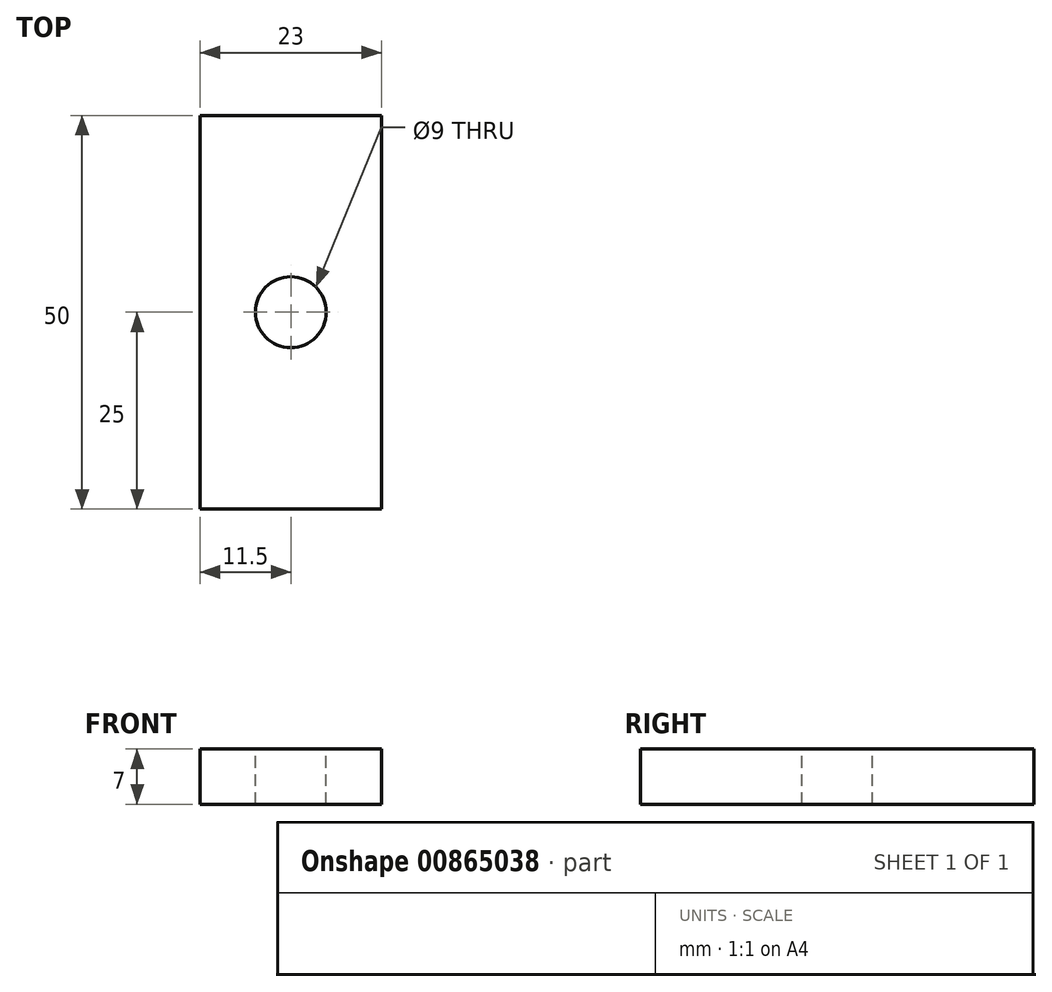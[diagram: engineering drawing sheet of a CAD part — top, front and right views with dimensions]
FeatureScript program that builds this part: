
annotation { "Feature Type Name" : "Feature", "Feature Type Description" : "" }
export const myFeature = defineFeature(function(context is Context, id is Id, definition is map)
    precondition{}
    {
        {
            var Q0;
            Q0=qCreatedBy(makeId("Top.planeOp"),FACE);
            var sketch = newSketch(context, id + "F0", { "sketchPlane" : qUnion([Q0])});
            skLineSegment(sketch, "E0.bottom", {"start": v(11.5, -25) * mm, "end": v(-11.5, -25) * mm});
            skLineSegment(sketch, "E0.top", {"start": v(11.5, 25) * mm, "end": v(-11.5, 25) * mm});
            skLineSegment(sketch, "E0.left", {"start": v(11.5, -25) * mm, "end": v(11.5, 25) * mm});
            skLineSegment(sketch, "E0.right", {"start": v(-11.5, -25) * mm, "end": v(-11.5, 25) * mm});
            skPoint(sketch, "E0.middle", {"position": v(0, 0) * mm});
            skSolve(sketch);
        }
        {
            var Q0;
            Q0=makeQuery(id+"F0.imprint","IMPRINT",FACE,{"disambiguationData":[TD([[makeQuery(id+"F0.imprint","IMPRINT",EDGE,{"derivedFrom":sQuery(id+"F0.wireOp",EDGE,"E0.bottom")}),-1.0]])]});
            extrude(context, id + "F1", {"entities" : qUnion([Q0]), "oppositeDirection" : true, "depth" : 15 * mm, "offsetDistance" : 25 * mm});
        }
        {
            var Q0;
            Q0=makeQuery(id+"F1.opExtrude","CAP_FACE",FACE,{"disambiguationData":[OSD([sQuery(id+"F0.wireOp",EDGE,"E0.bottom"),sQuery(id+"F0.wireOp",EDGE,"E0.top"),sQuery(id+"F0.wireOp",EDGE,"E0.left"),sQuery(id+"F0.wireOp",EDGE,"E0.right")])],"isStart":true});
            var sketch = newSketch(context, id + "F2", { "sketchPlane" : qUnion([Q0])});
            skCircle(sketch, "E1", {"center": v(0, 0) * mm, "radius": 14 * mm});
            skLineSegment(sketch, "E2", {"start": v(-14, 0) * mm, "end": v(14, 0) * mm});
            skSolve(sketch);
        }
        {
            var Q0;
            {var subQ0=sQuery(id+"F2.wireOp",EDGE,"E2");Q0=makeQuery(id+"F2.imprint","IMPRINT",FACE,{"disambiguationData":[TD([[makeQuery(id+"F2.imprint","IMPRINT",EDGE,{"derivedFrom":subQ0}),1.0]])]});}
            var Q1;
            Q1=sQuery(id+"F2.wireOp",EDGE,"E2");
            revolve(context, id + "F3", {"operationType" : NewBodyOperationType.REMOVE, "surfaceOperationType" : NewSurfaceOperationType.NEW, "entities" : qUnion([Q0]), "axis" : qUnion([Q1]), "revolveType" : RevolveType.FULL, "oppositeDirection" : true});
        }
        {
            var Q0;
            Q0=makeQuery(id+"F1.opExtrude","CAP_FACE",FACE,{"disambiguationData":[OSD([sQuery(id+"F0.wireOp",EDGE,"E0.bottom"),sQuery(id+"F0.wireOp",EDGE,"E0.top"),sQuery(id+"F0.wireOp",EDGE,"E0.left"),sQuery(id+"F0.wireOp",EDGE,"E0.right")])],"isStart":true});
            var sketch = newSketch(context, id + "F4", { "sketchPlane" : qUnion([Q0])});
            skCircle(sketch, "E3", {"center": v(0, 0) * mm, "radius": 4.5 * mm});
            skSolve(sketch);
        }
        {
            var Q0;
            Q0 = qSketchRegion(id + "F4", true);
            extrude(context, id + "F5", {"entities" : qUnion([Q0]), "operationType" : NewBodyOperationType.REMOVE, "oppositeDirection" : true, "depth" : 16 * mm, "offsetDistance" : 25 * mm});
        }
        {
            var Q0;
            Q0=makeQuery(id+"F1.opExtrude","CAP_FACE",FACE,{"disambiguationData":[OSD([sQuery(id+"F0.wireOp",EDGE,"E0.bottom"),sQuery(id+"F0.wireOp",EDGE,"E0.top"),sQuery(id+"F0.wireOp",EDGE,"E0.left"),sQuery(id+"F0.wireOp",EDGE,"E0.right")])],"isStart":true});
            var sketch = newSketch(context, id + "F6", { "sketchPlane" : qUnion([Q0])});
            skLineSegment(sketch, "E4.bottom", {"start": v(11.5, -25) * mm, "end": v(-11.5, -25) * mm});
            skLineSegment(sketch, "E4.top", {"start": v(11.5, 25) * mm, "end": v(-11.5, 25) * mm});
            skLineSegment(sketch, "E4.left", {"start": v(11.5, -25) * mm, "end": v(11.5, 25) * mm});
            skLineSegment(sketch, "E4.right", {"start": v(-11.5, -25) * mm, "end": v(-11.5, 25) * mm});
            skPoint(sketch, "E4.middle", {"position": v(0, 0) * mm});
            skSolve(sketch);
        }
        {
            var Q0;
            Q0 = qSketchRegion(id + "F6", true);
            extrude(context, id + "F7", {"entities" : qUnion([Q0]), "operationType" : NewBodyOperationType.REMOVE, "oppositeDirection" : true, "depth" : 8 * mm, "offsetDistance" : 25 * mm});
        }
    });
